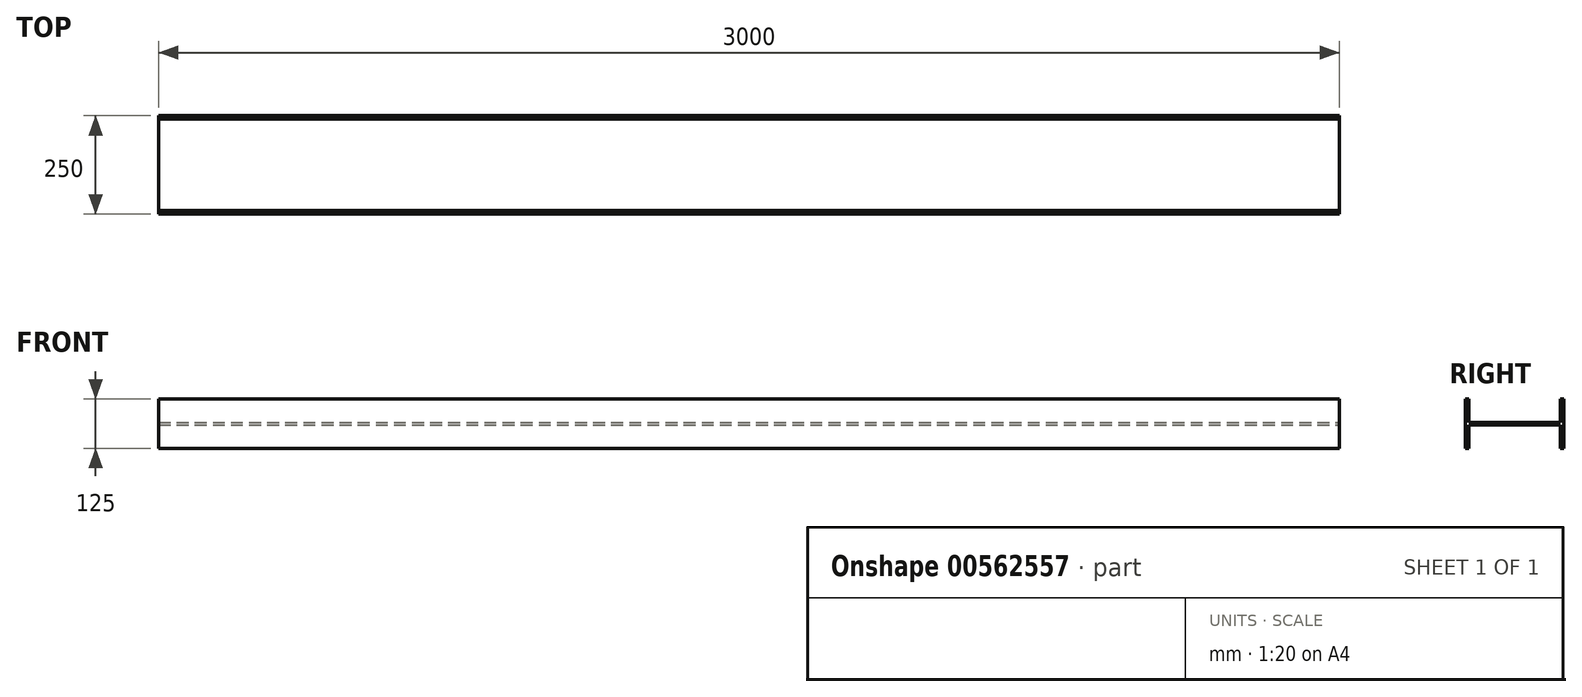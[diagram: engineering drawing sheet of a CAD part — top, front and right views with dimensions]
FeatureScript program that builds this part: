
annotation { "Feature Type Name" : "Feature", "Feature Type Description" : "" }
export const myFeature = defineFeature(function(context is Context, id is Id, definition is map)
    precondition{}
    {
        {
            var Q0;
            Q0=qCreatedBy(makeId("Top.planeOp"),FACE);
            var sketch = newSketch(context, id + "F0", { "sketchPlane" : qUnion([Q0])});
            skLineSegment(sketch, "E0", {"start": v(0, 250) * mm, "end": v(-62.5, 250) * mm});
            skLineSegment(sketch, "E1", {"start": v(-62.5, 250) * mm, "end": v(-62.5, 241) * mm});
            skLineSegment(sketch, "E2", {"start": v(-62.5, 241) * mm, "end": v(-3, 241) * mm});
            skLineSegment(sketch, "E3", {"start": v(-3, 241) * mm, "end": v(-3, 9) * mm});
            skLineSegment(sketch, "E4", {"start": v(-3, 9) * mm, "end": v(-62.5, 9) * mm});
            skLineSegment(sketch, "E5", {"start": v(-62.5, 9) * mm, "end": v(-62.5, 0) * mm});
            skLineSegment(sketch, "E6", {"start": v(-62.5, 0) * mm, "end": v(0, 0) * mm});
            skLineSegment(sketch, "E7.MirrorCS", {"start": v(62.5, 241) * mm, "end": v(3, 241) * mm});
            skLineSegment(sketch, "E8.MirrorCS", {"start": v(62.5, 0) * mm, "end": v(0, 0) * mm});
            skLineSegment(sketch, "E9.MirrorCS", {"start": v(3, 9) * mm, "end": v(62.5, 9) * mm});
            skLineSegment(sketch, "E10.MirrorCS", {"start": v(62.5, 9) * mm, "end": v(62.5, 0) * mm});
            skLineSegment(sketch, "E11.MirrorCS", {"start": v(3, 241) * mm, "end": v(3, 9) * mm});
            skLineSegment(sketch, "E12.MirrorCS", {"start": v(0, 250) * mm, "end": v(62.5, 250) * mm});
            skLineSegment(sketch, "E13.MirrorCS", {"start": v(62.5, 250) * mm, "end": v(62.5, 241) * mm});
            skSolve(sketch);
        }
        {
            var Q0;
            Q0=makeQuery(id+"F0.imprint","IMPRINT",FACE,{"disambiguationData":[TD([[makeQuery(id+"F0.imprint","IMPRINT",EDGE,{"derivedFrom":sQuery(id+"F0.wireOp",EDGE,"E0")}),1.0]])]});
            extrude(context, id + "F1", {"entities" : qUnion([Q0]), "depth" : 3000 * mm, "offsetDistance" : 25 * mm});
        }
        {
            var Q0;
            Q0=makeQuery(id+"F1.opExtrude","SWEPT_BODY",BODY,{"disambiguationData":[OSD([sQuery(id+"F0.wireOp",EDGE,"E0"),sQuery(id+"F0.wireOp",EDGE,"E1"),sQuery(id+"F0.wireOp",EDGE,"E2"),sQuery(id+"F0.wireOp",EDGE,"E3"),sQuery(id+"F0.wireOp",EDGE,"E4"),sQuery(id+"F0.wireOp",EDGE,"E5"),sQuery(id+"F0.wireOp",EDGE,"E6"),sQuery(id+"F0.wireOp",EDGE,"E7.MirrorCS"),sQuery(id+"F0.wireOp",EDGE,"E8.MirrorCS"),sQuery(id+"F0.wireOp",EDGE,"E9.MirrorCS"),sQuery(id+"F0.wireOp",EDGE,"E10.MirrorCS"),sQuery(id+"F0.wireOp",EDGE,"E11.MirrorCS"),sQuery(id+"F0.wireOp",EDGE,"E12.MirrorCS"),sQuery(id+"F0.wireOp",EDGE,"E13.MirrorCS")])]});
            var Q1;
            Q1=makeQuery(id+"F1.opExtrude","CAP_EDGE",EDGE,{"disambiguationData":[OSD([sQuery(id+"F0.wireOp",EDGE,"E5")])],"isStart":true});
            transform(context, id + "F2", {"entities" : qUnion([Q0]), "transformType" : TransformType.ROTATION, "transformAxis" : qUnion([Q1]), "angle" : 90 * degree, "makeCopy" : false});
        }
    });
